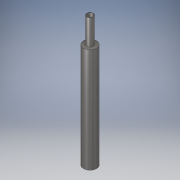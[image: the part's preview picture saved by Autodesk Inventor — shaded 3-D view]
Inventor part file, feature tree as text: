
AUTODESK INVENTOR PART (.ipt)
format: ipt  version: 2018 (Build 220112000, 112)  size: 112,128 bytes
history: native  units: in
note: dims shown in document units (in); Inventor stores cm internally (conversion verified against a paired STEP export)
features: extrude x3, sketch x3
ambient origin geometry x8: Origin, YZ Plane, XZ Plane, XY Plane, X Axis, Y Axis, Z Axis, Center Point
bodies: Solid1 (feature_tree)
feature tree (6):
  extrude  "Extrusion1"  Depth=0.5in
  extrude  "Extrusion2"  Depth=2.0in
  extrude  "Extrusion3"  Depth=8.0in
  sketch  "Sketch1"  dims[d0=0.5in d1=0.025in]
  sketch  "Sketch2"  dims[d2=2.0in d3=0.0in d4=0.95in]
  sketch  "Sketch3"  dims[d5=0.05in d6=0.0in d7=1.0in d8=8.0in d9=0.0in]
